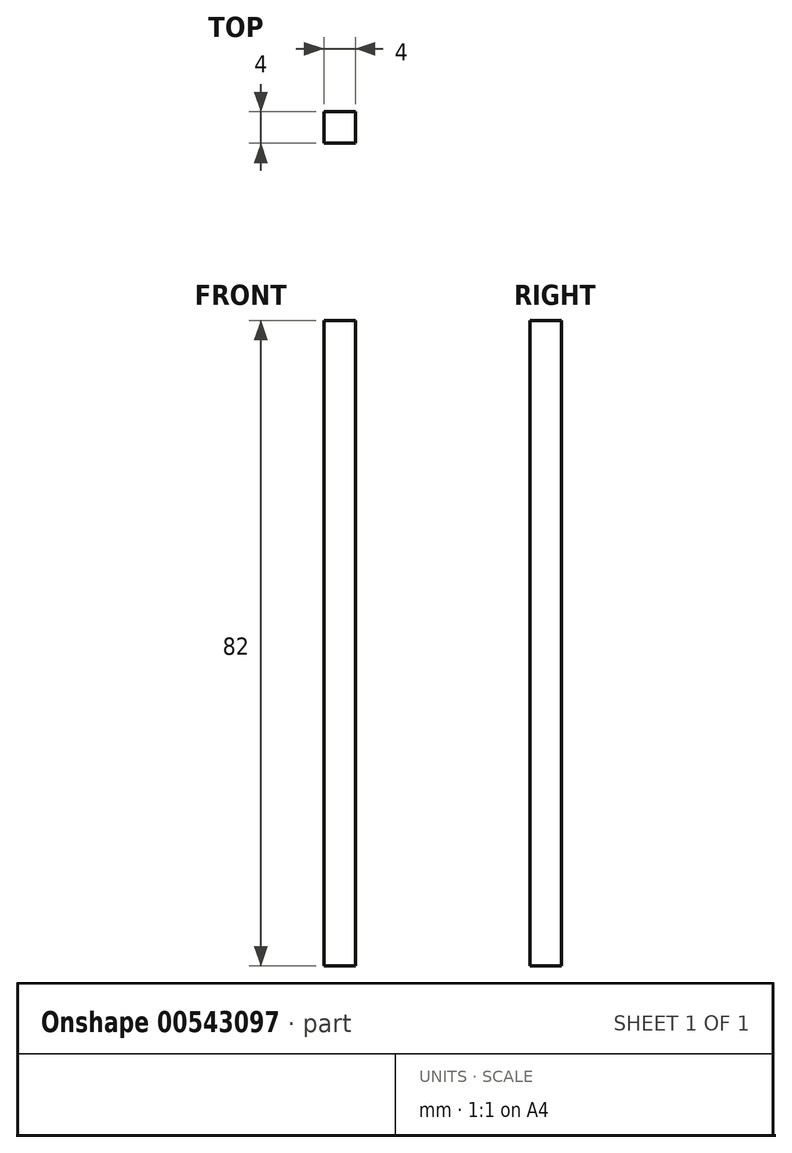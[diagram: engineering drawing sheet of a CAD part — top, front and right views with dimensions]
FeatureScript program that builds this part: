
annotation { "Feature Type Name" : "Feature", "Feature Type Description" : "" }
export const myFeature = defineFeature(function(context is Context, id is Id, definition is map)
    precondition{}
    {
        {
            var Q0;
            Q0=qCreatedBy(makeId("Top.planeOp"),FACE);
            var sketch = newSketch(context, id + "F0", { "sketchPlane" : qUnion([Q0])});
            skLineSegment(sketch, "E0.bottom", {"start": v(0, 0) * mm, "end": v(4, 0) * mm});
            skLineSegment(sketch, "E0.top", {"start": v(0, 4) * mm, "end": v(4, 4) * mm});
            skLineSegment(sketch, "E0.left", {"start": v(0, 0) * mm, "end": v(0, 4) * mm});
            skLineSegment(sketch, "E0.right", {"start": v(4, 0) * mm, "end": v(4, 4) * mm});
            skSolve(sketch);
        }
        {
            var Q0;
            Q0 = qSketchRegion(id + "F0", true);
            extrude(context, id + "F1", {"entities" : qUnion([Q0]), "depth" : 82 * mm, "offsetDistance" : 25 * mm});
        }
    });
